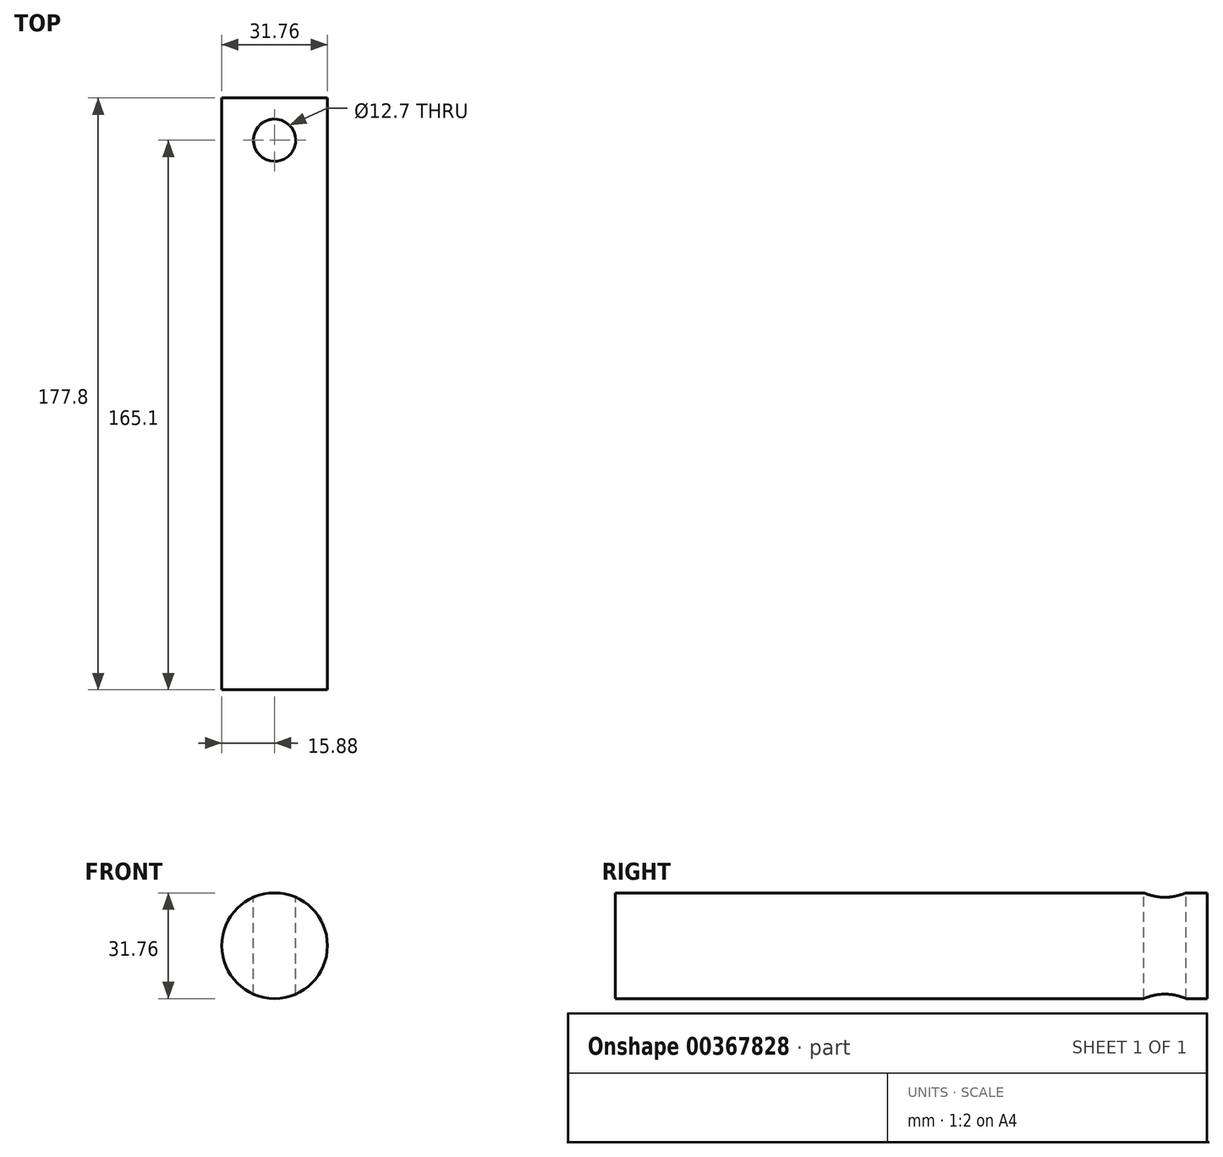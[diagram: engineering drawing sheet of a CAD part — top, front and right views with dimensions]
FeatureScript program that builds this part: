
annotation { "Feature Type Name" : "Feature", "Feature Type Description" : "" }
export const myFeature = defineFeature(function(context is Context, id is Id, definition is map)
    precondition{}
    {
        {
            var Q0;
            Q0=qCreatedBy(makeId("Front.planeOp"),FACE);
            var sketch = newSketch(context, id + "F0", { "sketchPlane" : qUnion([Q0])});
            skCircle(sketch, "E0", {"center": v(0, 0) * mm, "radius": 15.88 * mm});
            skSolve(sketch);
        }
        {
            var Q0;
            Q0 = qSketchRegion(id + "F0", true);
            extrude(context, id + "F1", {"entities" : qUnion([Q0]), "depth" : 177.8 * mm});
        }
        {
            var Q0;
            Q0=qCreatedBy(makeId("Top.planeOp"),FACE);
            var sketch = newSketch(context, id + "F2", { "sketchPlane" : qUnion([Q0])});
            skCircle(sketch, "E1", {"center": v(0, -12.7) * mm, "radius": 6.35 * mm});
            skSolve(sketch);
        }
        {
            var Q0;
            Q0 = qSketchRegion(id + "F2", true);
            extrude(context, id + "F3", {"entities" : qUnion([Q0]), "operationType" : NewBodyOperationType.REMOVE, "endBound" : BoundingType.THROUGH_ALL, "oppositeDirection" : true, "depth" : 25.4 * mm, "hasSecondDirection" : true, "secondDirectionOppositeDirection" : false, "secondDirectionDepth" : 25.4 * mm});
        }
    });
